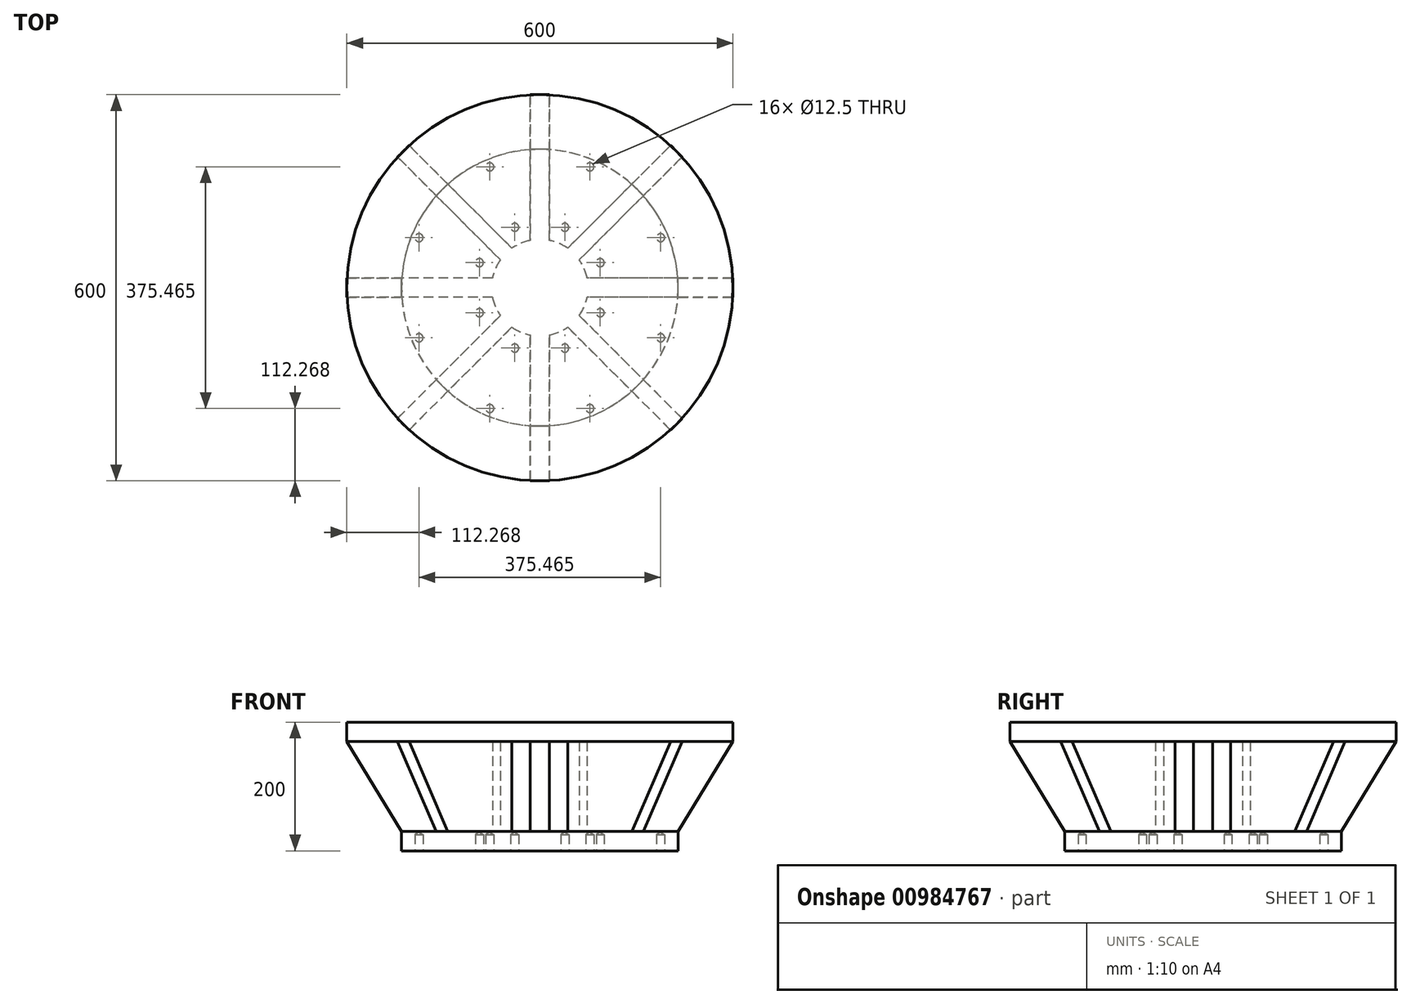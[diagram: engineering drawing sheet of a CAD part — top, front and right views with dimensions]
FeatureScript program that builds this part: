
annotation { "Feature Type Name" : "Feature", "Feature Type Description" : "" }
export const myFeature = defineFeature(function(context is Context, id is Id, definition is map)
    precondition{}
    {
        {
            var Q0;
            Q0=qCreatedBy(makeId("Right.planeOp"),FACE);
            var sketch = newSketch(context, id + "F0", { "sketchPlane" : qUnion([Q0])});
            skLineSegment(sketch, "E0.bottom", {"start": v(215, 15) * mm, "end": v(-215, 15) * mm});
            skLineSegment(sketch, "E0.top", {"start": v(215, -15) * mm, "end": v(-215, -15) * mm});
            skLineSegment(sketch, "E0.left", {"start": v(215, 15) * mm, "end": v(215, -15) * mm});
            skLineSegment(sketch, "E0.right", {"start": v(-215, 15) * mm, "end": v(-215, -15) * mm});
            skPoint(sketch, "E0.middle", {"position": v(0, 0) * mm});
            skLineSegment(sketch, "E1", {"start": v(-215, 15) * mm, "end": v(-300, 155) * mm});
            skLineSegment(sketch, "E2", {"start": v(-300, 155) * mm, "end": v(300, 155) * mm});
            skLineSegment(sketch, "E3", {"start": v(300, 155) * mm, "end": v(215, 15) * mm});
            skLineSegment(sketch, "E4", {"start": v(0, -15) * mm, "end": v(0, 15) * mm});
            skLineSegment(sketch, "E5", {"start": v(0, 15) * mm, "end": v(0, 155) * mm});
            skLineSegment(sketch, "E6.top", {"start": v(-300, 185) * mm, "end": v(300, 185) * mm});
            skLineSegment(sketch, "E6.left", {"start": v(-300, 155) * mm, "end": v(-300, 185) * mm});
            skLineSegment(sketch, "E6.right", {"start": v(300, 155) * mm, "end": v(300, 185) * mm});
            skLineSegment(sketch, "E7", {"start": v(0, 155) * mm, "end": v(0, 185) * mm});
            skSolve(sketch);
        }
        {
            var Q0;
            {var subQ0=sQuery(id+"F0.wireOp",EDGE,"E0.left");Q0=makeQuery(id+"F0.imprint","IMPRINT",FACE,{"disambiguationData":[TD([[makeQuery(id+"F0.imprint","IMPRINT",EDGE,{"derivedFrom":subQ0}),-1.0]])]});}
            var Q1;
            Q1=sQuery(id+"F0.wireOp",EDGE,"E4");
            revolve(context, id + "F1", {"surfaceOperationType" : NewSurfaceOperationType.NEW, "entities" : qUnion([Q0]), "axis" : qUnion([Q1]), "revolveType" : RevolveType.FULL});
        }
        {
            var Q0;
            {var subQ0=sQuery(id+"F0.wireOp",EDGE,"E6.right");Q0=makeQuery(id+"F0.imprint","IMPRINT",FACE,{"disambiguationData":[TD([[makeQuery(id+"F0.imprint","IMPRINT",EDGE,{"derivedFrom":subQ0}),1.0]])]});}
            var Q1;
            Q1=sQuery(id+"F0.wireOp",EDGE,"E7");
            revolve(context, id + "F2", {"operationType" : NewBodyOperationType.ADD, "surfaceOperationType" : NewSurfaceOperationType.NEW, "entities" : qUnion([Q0]), "axis" : qUnion([Q1]), "revolveType" : RevolveType.FULL});
        }
        {
            var Q0;
            {var subQ0=sQuery(id+"F0.wireOp",EDGE,"E1");Q0=makeQuery(id+"F0.imprint","IMPRINT",FACE,{"disambiguationData":[TD([[makeQuery(id+"F0.imprint","IMPRINT",EDGE,{"derivedFrom":subQ0}),-1.0]])]});}
            var Q1;
            {var subQ0=sQuery(id+"F0.wireOp",EDGE,"E3");Q1=makeQuery(id+"F0.imprint","IMPRINT",FACE,{"disambiguationData":[TD([[makeQuery(id+"F0.imprint","IMPRINT",EDGE,{"derivedFrom":subQ0}),-1.0]])]});}
            extrude(context, id + "F3", {"entities" : qUnion([Q0, Q1]), "operationType" : NewBodyOperationType.ADD, "endBound" : BoundingType.SYMMETRIC, "depth" : 30 * mm, "offsetDistance" : 25.4 * mm});
        }
        {
            var Q0;
            Q0=qCreatedBy(makeId("Front.planeOp"),FACE);
            var sketch = newSketch(context, id + "F4", { "sketchPlane" : qUnion([Q0])});
            skLineSegment(sketch, "E8.bottom", {"start": v(215, 15) * mm, "end": v(-215, 15) * mm});
            skLineSegment(sketch, "E8.top", {"start": v(215, -15) * mm, "end": v(-215, -15) * mm});
            skLineSegment(sketch, "E8.left", {"start": v(215, 15) * mm, "end": v(215, -15) * mm});
            skLineSegment(sketch, "E8.right", {"start": v(-215, 15) * mm, "end": v(-215, -15) * mm});
            skPoint(sketch, "E8.middle", {"position": v(0, 0) * mm});
            skLineSegment(sketch, "E9", {"start": v(215, 15) * mm, "end": v(300, 155) * mm});
            skLineSegment(sketch, "E10", {"start": v(300, 155) * mm, "end": v(-300, 155) * mm});
            skLineSegment(sketch, "E11", {"start": v(-300, 155) * mm, "end": v(-215, 15) * mm});
            skLineSegment(sketch, "E12", {"start": v(0, 0) * mm, "end": v(0, 155) * mm});
            skSolve(sketch);
        }
        {
            var Q0;
            {var subQ0=sQuery(id+"F4.wireOp",EDGE,"E9");Q0=makeQuery(id+"F4.imprint","IMPRINT",FACE,{"disambiguationData":[TD([[makeQuery(id+"F4.imprint","IMPRINT",EDGE,{"derivedFrom":subQ0}),1.0]])]});}
            var Q1;
            {var subQ0=sQuery(id+"F4.wireOp",EDGE,"E11");Q1=makeQuery(id+"F4.imprint","IMPRINT",FACE,{"disambiguationData":[TD([[makeQuery(id+"F4.imprint","IMPRINT",EDGE,{"derivedFrom":subQ0}),1.0]])]});}
            extrude(context, id + "F5", {"entities" : qUnion([Q0, Q1]), "operationType" : NewBodyOperationType.ADD, "endBound" : BoundingType.SYMMETRIC, "depth" : 30 * mm, "offsetDistance" : 25.4 * mm});
        }
        {
            var Q0;
            Q0=sQuery(id+"F0.wireOp",EDGE,"E5");
            cPlane(context, id + "F6", {"entities" : qUnion([Q0]), "cplaneType" : CPlaneType.LINE_ANGLE, "offset" : 25.4 * mm, "angle" : 45 * degree, "width" : 152.4 * mm, "height" : 152.4 * mm});
        }
        {
            var Q0;
            Q0=qCreatedBy(id+"F6.planeOp",FACE);
            var sketch = newSketch(context, id + "F7", { "sketchPlane" : qUnion([Q0])});
            skLineSegment(sketch, "E13.bottom", {"start": v(215, 15) * mm, "end": v(-215, 15) * mm});
            skLineSegment(sketch, "E13.top", {"start": v(215, -15) * mm, "end": v(-215, -15) * mm});
            skLineSegment(sketch, "E13.left", {"start": v(215, 15) * mm, "end": v(215, -15) * mm});
            skLineSegment(sketch, "E13.right", {"start": v(-215, 15) * mm, "end": v(-215, -15) * mm});
            skPoint(sketch, "E13.middle", {"position": v(0, 0) * mm});
            skLineSegment(sketch, "E14", {"start": v(-215, 15) * mm, "end": v(-300, 155) * mm});
            skLineSegment(sketch, "E15", {"start": v(-300, 155) * mm, "end": v(300, 155) * mm});
            skLineSegment(sketch, "E16", {"start": v(300, 155) * mm, "end": v(215, 15) * mm});
            skSolve(sketch);
        }
        {
            var Q0;
            Q0=makeQuery(id+"F7.imprint","IMPRINT",FACE,{"disambiguationData":[TD([[makeQuery(id+"F7.imprint","IMPRINT",EDGE,{"derivedFrom":sQuery(id+"F7.wireOp",EDGE,"E13.bottom")}),-1.0]])]});
            extrude(context, id + "F8", {"entities" : qUnion([Q0]), "operationType" : NewBodyOperationType.ADD, "endBound" : BoundingType.SYMMETRIC, "depth" : 25.4 * mm, "offsetDistance" : 25.4 * mm});
        }
        {
            var Q0;
            Q0=sQuery(id+"F0.wireOp",EDGE,"E5");
            cPlane(context, id + "F9", {"entities" : qUnion([Q0]), "cplaneType" : CPlaneType.LINE_ANGLE, "offset" : 25.4 * mm, "angle" : 45 * degree, "oppositeDirection" : true, "width" : 152.4 * mm, "height" : 152.4 * mm});
        }
        {
            var Q0;
            Q0=qCreatedBy(id+"F9.planeOp",FACE);
            var sketch = newSketch(context, id + "F10", { "sketchPlane" : qUnion([Q0])});
            skLineSegment(sketch, "E17.bottom", {"start": v(215, 15) * mm, "end": v(-215, 15) * mm});
            skLineSegment(sketch, "E17.top", {"start": v(215, -15) * mm, "end": v(-215, -15) * mm});
            skLineSegment(sketch, "E17.left", {"start": v(215, 15) * mm, "end": v(215, -15) * mm});
            skLineSegment(sketch, "E17.right", {"start": v(-215, 15) * mm, "end": v(-215, -15) * mm});
            skPoint(sketch, "E17.middle", {"position": v(0, 0) * mm});
            skLineSegment(sketch, "E18", {"start": v(-215, 15) * mm, "end": v(-300, 155) * mm});
            skLineSegment(sketch, "E19", {"start": v(-300, 155) * mm, "end": v(300, 155) * mm});
            skLineSegment(sketch, "E20", {"start": v(300, 155) * mm, "end": v(215, 15) * mm});
            skSolve(sketch);
        }
        {
            var Q0;
            Q0=makeQuery(id+"F10.imprint","IMPRINT",FACE,{"disambiguationData":[TD([[makeQuery(id+"F10.imprint","IMPRINT",EDGE,{"derivedFrom":sQuery(id+"F10.wireOp",EDGE,"E17.bottom")}),-1.0]])]});
            extrude(context, id + "F11", {"entities" : qUnion([Q0]), "operationType" : NewBodyOperationType.ADD, "endBound" : BoundingType.SYMMETRIC, "depth" : 25.4 * mm, "offsetDistance" : 25.4 * mm});
        }
        {
            var Q0;
            Q0=makeQuery(id+"F1.opRevolve","SWEPT_FACE",FACE,{"disambiguationData":[OSD([sQuery(id+"F0.wireOp",EDGE,"E0.top")])]});
            var sketch = newSketch(context, id + "F12", { "sketchPlane" : qUnion([Q0])});
            skCircle(sketch, "E21", {"center": v(0, 0) * mm, "radius": 101.6 * mm});
            skCircle(sketch, "E22", {"center": v(0, 0) * mm, "radius": 203.2 * mm});
            skLineSegment(sketch, "E23", {"start": v(0, 0) * mm, "end": v(82.28, 198.63) * mm});
            skLineSegment(sketch, "E24", {"start": v(0, 0) * mm, "end": v(215, 0) * mm});
            skLineSegment(sketch, "E25", {"start": v(0, 0) * mm, "end": v(198.63, 82.28) * mm});
            skLineSegment(sketch, "E26", {"start": v(0, 0) * mm, "end": v(198.63, -82.28) * mm});
            skLineSegment(sketch, "E27", {"start": v(0, 0) * mm, "end": v(82.28, -198.63) * mm});
            skLineSegment(sketch, "E28", {"start": v(0, 0) * mm, "end": v(-82.28, -198.63) * mm});
            skLineSegment(sketch, "E29", {"start": v(0, 0) * mm, "end": v(-198.63, -82.28) * mm});
            skLineSegment(sketch, "E30", {"start": v(0, 0) * mm, "end": v(-198.63, 82.28) * mm});
            skLineSegment(sketch, "E31", {"start": v(0, 0) * mm, "end": v(-82.28, 198.63) * mm});
            skPoint(sketch, "E32", {"position": v(-77.76, 187.73) * mm});
            skPoint(sketch, "E33", {"position": v(77.76, 187.73) * mm});
            skPoint(sketch, "E34", {"position": v(187.73, 77.76) * mm});
            skPoint(sketch, "E35", {"position": v(187.73, -77.76) * mm});
            skPoint(sketch, "E36", {"position": v(77.76, -187.73) * mm});
            skPoint(sketch, "E37", {"position": v(-77.76, -187.73) * mm});
            skPoint(sketch, "E38", {"position": v(-187.73, -77.76) * mm});
            skPoint(sketch, "E39", {"position": v(-187.73, 77.76) * mm});
            skPoint(sketch, "E40", {"position": v(-38.88, 93.87) * mm});
            skPoint(sketch, "E41", {"position": v(38.88, 93.87) * mm});
            skPoint(sketch, "E42", {"position": v(-38.88, -93.87) * mm});
            skPoint(sketch, "E43", {"position": v(38.88, -93.87) * mm});
            skPoint(sketch, "E44", {"position": v(93.87, -38.88) * mm});
            skPoint(sketch, "E45", {"position": v(93.87, 38.88) * mm});
            skPoint(sketch, "E46", {"position": v(-93.87, 38.88) * mm});
            skPoint(sketch, "E47", {"position": v(-93.87, -38.88) * mm});
            skSolve(sketch);
        }
        {
            var Q0;
            Q0=sQuery(id+"F12.wireOp",VERTEX,"E39");
            var Q1;
            Q1=sQuery(id+"F12.wireOp",VERTEX,"E32");
            var Q2;
            Q2=sQuery(id+"F12.wireOp",VERTEX,"E33");
            var Q3;
            Q3=sQuery(id+"F12.wireOp",VERTEX,"E34");
            var Q4;
            Q4=sQuery(id+"F12.wireOp",VERTEX,"E35");
            var Q5;
            Q5=sQuery(id+"F12.wireOp",VERTEX,"E36");
            var Q6;
            Q6=sQuery(id+"F12.wireOp",VERTEX,"E37");
            var Q7;
            Q7=sQuery(id+"F12.wireOp",VERTEX,"E38");
            var Q8;
            Q8=sQuery(id+"F12.wireOp",VERTEX,"E47");
            var Q9;
            Q9=sQuery(id+"F12.wireOp",VERTEX,"E42");
            var Q10;
            Q10=sQuery(id+"F12.wireOp",VERTEX,"E43");
            var Q11;
            Q11=sQuery(id+"F12.wireOp",VERTEX,"E44");
            var Q12;
            Q12=sQuery(id+"F12.wireOp",VERTEX,"E45");
            var Q13;
            Q13=sQuery(id+"F12.wireOp",VERTEX,"E41");
            var Q14;
            Q14=sQuery(id+"F12.wireOp",VERTEX,"E40");
            var Q15;
            Q15=sQuery(id+"F12.wireOp",VERTEX,"E46");
            var Q16;
            Q16=makeQuery(id+"F1.opRevolve","SWEPT_BODY",BODY,{"disambiguationData":[OSD([sQuery(id+"F0.wireOp",EDGE,"E0.bottom"),sQuery(id+"F0.wireOp",EDGE,"E0.top"),sQuery(id+"F0.wireOp",EDGE,"E0.left"),sQuery(id+"F0.wireOp",EDGE,"E4")])]});
            hole(context, id + "F13", {"style" : HoleStyle.SIMPLE, "endStyle" : HoleEndStyle.BLIND, "holeDiameter" : 12.5 * mm, "majorDiameter" : 6.35 * mm, "holeDepth" : 25.4 * mm, "isTappedThrough" : true, "tappedDepth" : 12.7 * mm, "tapClearance" : 3, "locations" : qUnion([Q0, Q1, Q2, Q3, Q4, Q5, Q6, Q7, Q8, Q9, Q10, Q11, Q12, Q13, Q14, Q15]), "scope" : qUnion([Q16])});
        }
        {
            var Q0;
            Q0=makeQuery(id+"F1.opRevolve","SWEPT_FACE",FACE,{"disambiguationData":[OSD([sQuery(id+"F0.wireOp",EDGE,"E0.top")])]});
            var sketch = newSketch(context, id + "F14", { "sketchPlane" : qUnion([Q0])});
            skCircle(sketch, "E48", {"center": v(0, 0) * mm, "radius": 75 * mm});
            skSolve(sketch);
        }
        {
            var Q0;
            Q0=makeQuery(id+"F14.imprint","IMPRINT",FACE,{"disambiguationData":[TD([[makeQuery(id+"F14.imprint","IMPRINT",EDGE,{"derivedFrom":sQuery(id+"F14.wireOp",EDGE,"E48")}),1.0]])]});
            extrude(context, id + "F15", {"entities" : qUnion([Q0]), "operationType" : NewBodyOperationType.ADD, "oppositeDirection" : true, "depth" : 200 * mm, "offsetDistance" : 25.4 * mm});
        }
    });
